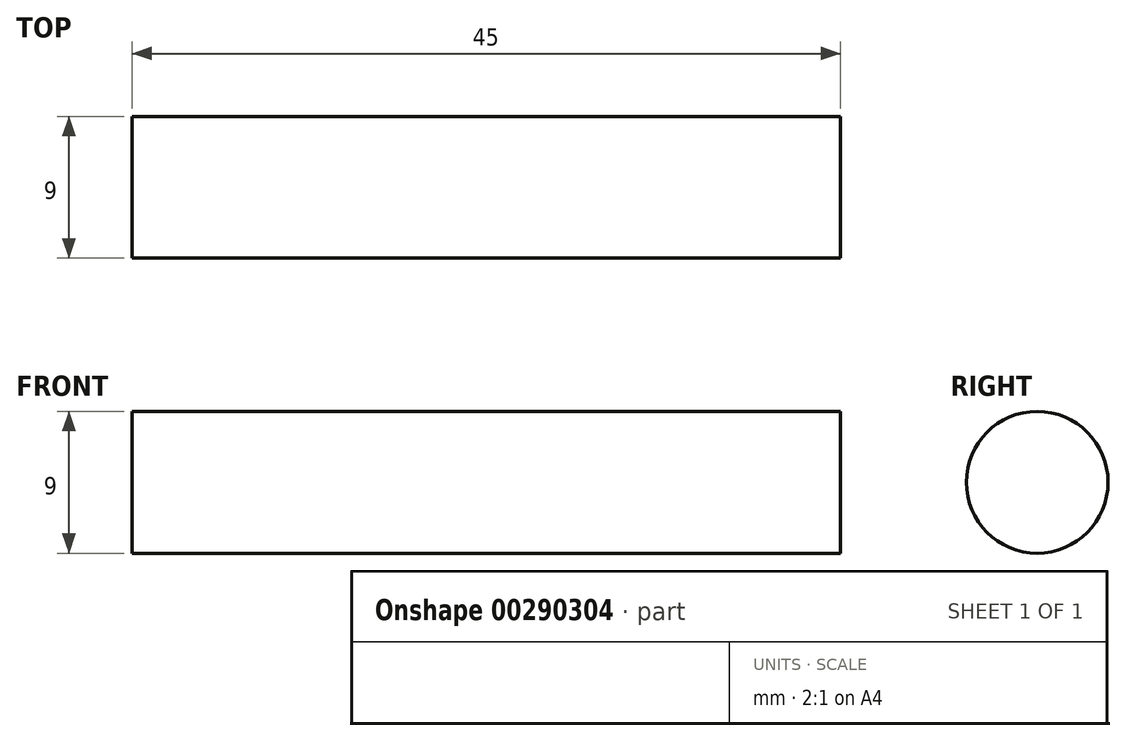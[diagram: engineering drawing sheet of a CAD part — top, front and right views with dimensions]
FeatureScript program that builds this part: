
annotation { "Feature Type Name" : "Feature", "Feature Type Description" : "" }
export const myFeature = defineFeature(function(context is Context, id is Id, definition is map)
    precondition{}
    {
        {
            var Q0;
            Q0=qCreatedBy(makeId("Front.planeOp"),FACE);
            var sketch = newSketch(context, id + "F0", { "sketchPlane" : qUnion([Q0])});
            skLineSegment(sketch, "E0", {"start": v(0, 4.5) * mm, "end": v(22.5, 4.5) * mm});
            skLineSegment(sketch, "E1", {"start": v(22.5, 4.5) * mm, "end": v(22.5, 0) * mm});
            skLineSegment(sketch, "E2.MirrorCS", {"start": v(-22.5, 4.5) * mm, "end": v(-22.5, 0) * mm});
            skLineSegment(sketch, "E3.MirrorCS", {"start": v(0, 4.5) * mm, "end": v(-22.5, 4.5) * mm});
            skLineSegment(sketch, "E4", {"start": v(-22.5, 0) * mm, "end": v(22.5, 0) * mm});
            skSolve(sketch);
        }
        {
            var Q0;
            Q0=makeQuery(id+"F0.imprint","IMPRINT",FACE,{"disambiguationData":[TD([[makeQuery(id+"F0.imprint","IMPRINT",EDGE,{"derivedFrom":sQuery(id+"F0.wireOp",EDGE,"E0")}),-1.0]])]});
            var Q1;
            Q1=sQuery(id+"F0.wireOp",EDGE,"E4");
            revolve(context, id + "F1", {"entities" : qUnion([Q0]), "axis" : qUnion([Q1]), "revolveType" : RevolveType.FULL});
        }
    });
